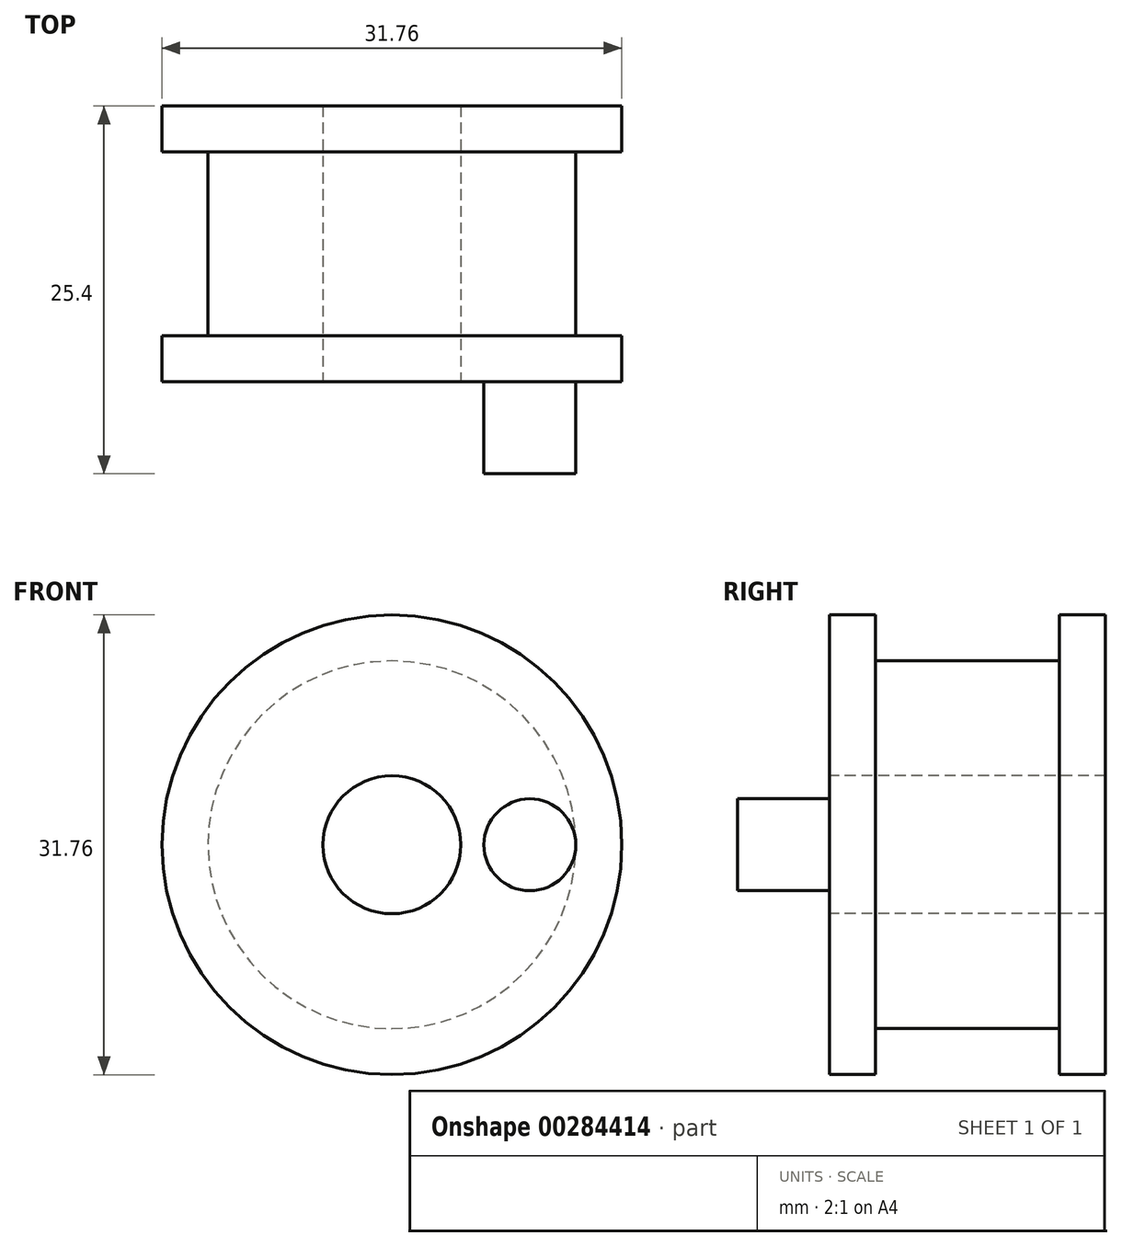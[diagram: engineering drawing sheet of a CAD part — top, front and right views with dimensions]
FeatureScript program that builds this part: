
annotation { "Feature Type Name" : "Feature", "Feature Type Description" : "" }
export const myFeature = defineFeature(function(context is Context, id is Id, definition is map)
    precondition{}
    {
        {
            var Q0;
            Q0=qCreatedBy(makeId("Right.planeOp"),FACE);
            var sketch = newSketch(context, id + "F0", { "sketchPlane" : qUnion([Q0])});
            skLineSegment(sketch, "E0", {"start": v(0, 0) * mm, "end": v(19.05, 0) * mm});
            skLineSegment(sketch, "E1", {"start": v(19.05, 4.76) * mm, "end": v(0, 4.76) * mm});
            skLineSegment(sketch, "E2", {"start": v(19.05, 4.76) * mm, "end": v(19.05, 15.88) * mm});
            skLineSegment(sketch, "E3", {"start": v(0, 4.76) * mm, "end": v(0, 15.88) * mm});
            skLineSegment(sketch, "E4", {"start": v(0, 15.88) * mm, "end": v(3.17, 15.88) * mm});
            skLineSegment(sketch, "E5", {"start": v(3.17, 15.88) * mm, "end": v(3.17, 4.76) * mm});
            skLineSegment(sketch, "E6.MirrorCS", {"start": v(15.88, 15.88) * mm, "end": v(15.88, 4.76) * mm});
            skLineSegment(sketch, "E7", {"start": v(15.88, 15.88) * mm, "end": v(19.05, 15.88) * mm});
            skLineSegment(sketch, "E8", {"start": v(3.17, 12.7) * mm, "end": v(15.88, 12.7) * mm});
            skSolve(sketch);
        }
        {
            var Q0;
            {var subQ5=sQuery(id+"F0.wireOp",EDGE,"E8");Q0=makeQuery(id+"F0.imprint","IMPRINT",FACE,{"disambiguationData":[TD([[makeQuery(id+"F0.imprint","IMPRINT",EDGE,{"derivedFrom":subQ5}),-1.0]])]});}
            var Q1;
            {var subQ3=sQuery(id+"F0.wireOp",EDGE,"E3");Q1=makeQuery(id+"F0.imprint","IMPRINT",FACE,{"disambiguationData":[TD([[makeQuery(id+"F0.imprint","IMPRINT",EDGE,{"derivedFrom":subQ3}),-1.0]])]});}
            var Q2;
            {var subQ5=sQuery(id+"F0.wireOp",EDGE,"E2");Q2=makeQuery(id+"F0.imprint","IMPRINT",FACE,{"disambiguationData":[TD([[makeQuery(id+"F0.imprint","IMPRINT",EDGE,{"derivedFrom":subQ5}),1.0]])]});}
            var Q3;
            Q3=sQuery(id+"F0.wireOp",EDGE,"E0");
            revolve(context, id + "F1", {"entities" : qUnion([Q0, Q1, Q2]), "axis" : qUnion([Q3]), "revolveType" : RevolveType.FULL});
        }
        {
            var Q0;
            Q0=qCreatedBy(makeId("Front.planeOp"),FACE);
            var sketch = newSketch(context, id + "F2", { "sketchPlane" : qUnion([Q0])});
            skCircle(sketch, "E9", {"center": v(9.53, 0) * mm, "radius": 3.18 * mm});
            skSolve(sketch);
        }
        {
            var Q0;
            Q0=makeQuery(id+"F2.imprint","IMPRINT",FACE,{"disambiguationData":[TD([[makeQuery(id+"F2.imprint","IMPRINT",EDGE,{"derivedFrom":sQuery(id+"F2.wireOp",EDGE,"E9")}),1.0]])]});
            extrude(context, id + "F3", {"entities" : qUnion([Q0]), "operationType" : NewBodyOperationType.ADD, "depth" : 6.35 * mm});
        }
    });
